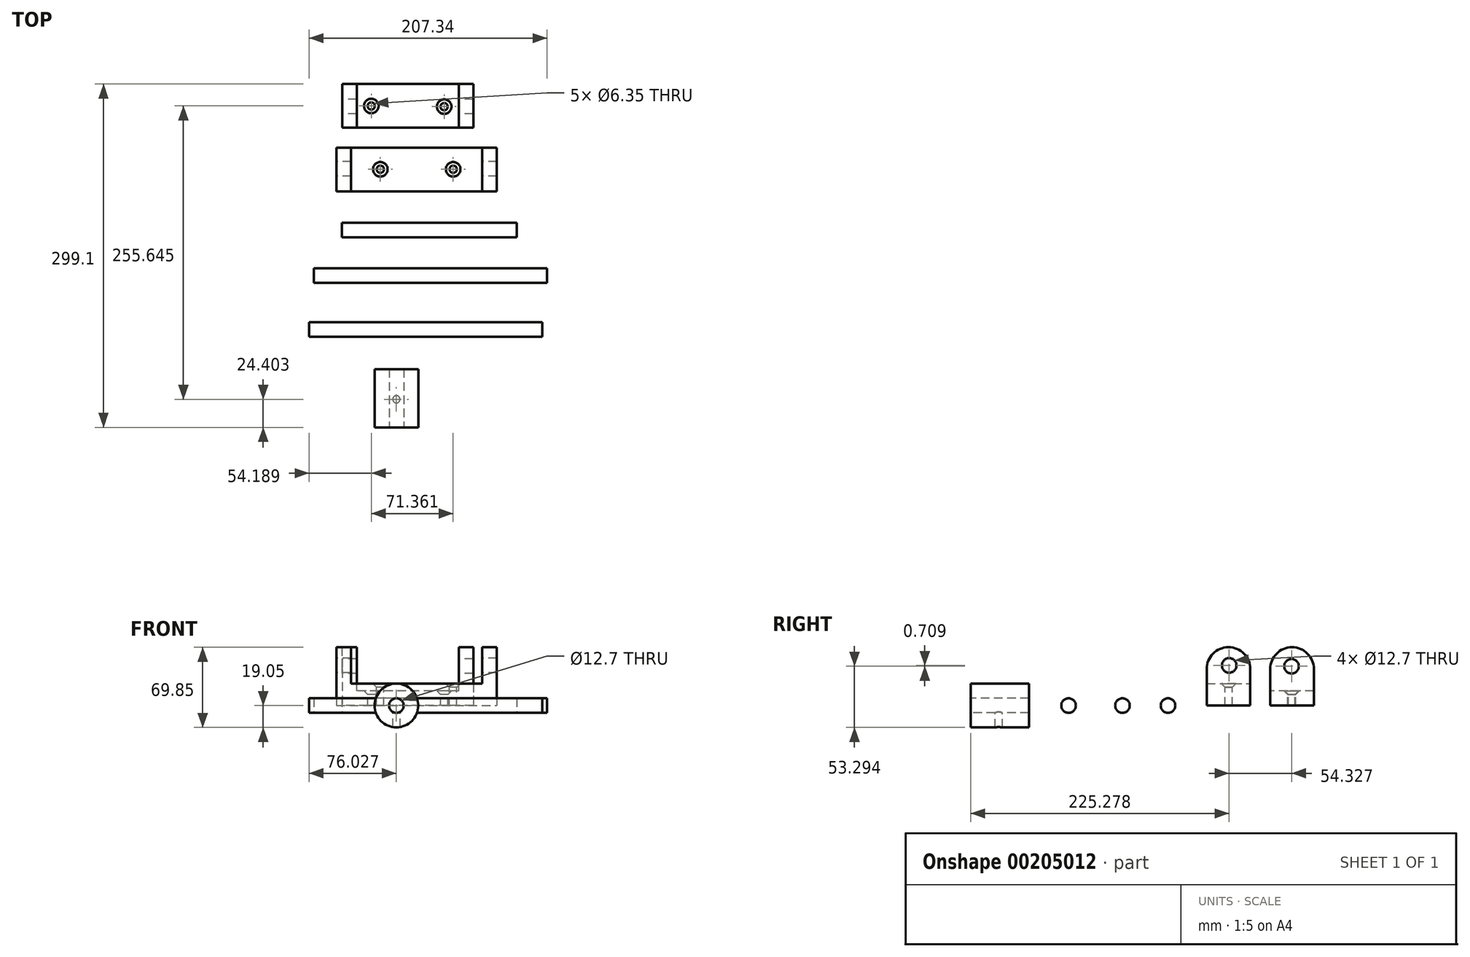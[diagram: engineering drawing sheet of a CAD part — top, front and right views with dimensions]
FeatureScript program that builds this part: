
annotation { "Feature Type Name" : "Feature", "Feature Type Description" : "" }
export const myFeature = defineFeature(function(context is Context, id is Id, definition is map)
    precondition{}
    {
        {
            var Q0;
            Q0=qCreatedBy(makeId("Top.planeOp"),FACE);
            var sketch = newSketch(context, id + "F0", { "sketchPlane" : qUnion([Q0])});
            skLineSegment(sketch, "E0.bottom", {"start": v(0, 38.1) * mm, "end": v(139.7, 38.1) * mm});
            skLineSegment(sketch, "E0.top", {"start": v(0, 0) * mm, "end": v(139.7, 0) * mm});
            skLineSegment(sketch, "E0.left", {"start": v(0, 38.1) * mm, "end": v(0, 0) * mm});
            skLineSegment(sketch, "E0.right", {"start": v(139.7, 38.1) * mm, "end": v(139.7, 0) * mm});
            skSolve(sketch);
        }
        {
            var Q0;
            Q0 = qSketchRegion(id + "F0", true);
            extrude(context, id + "F1", {"entities" : qUnion([Q0]), "depth" : 50.8 * mm});
        }
        {
            var Q0;
            Q0=makeQuery(id+"F1.opExtrude","CAP_FACE",FACE,{"disambiguationData":[OSD([sQuery(id+"F0.wireOp",EDGE,"E0.bottom"),sQuery(id+"F0.wireOp",EDGE,"E0.top"),sQuery(id+"F0.wireOp",EDGE,"E0.left"),sQuery(id+"F0.wireOp",EDGE,"E0.right")])],"isStart":false});
            var sketch = newSketch(context, id + "F2", { "sketchPlane" : qUnion([Q0])});
            skLineSegment(sketch, "E1.bottom", {"start": v(12.7, 0) * mm, "end": v(127, 0) * mm});
            skLineSegment(sketch, "E1.top", {"start": v(12.7, 38.1) * mm, "end": v(127, 38.1) * mm});
            skLineSegment(sketch, "E1.left", {"start": v(12.7, 0) * mm, "end": v(12.7, 38.1) * mm});
            skLineSegment(sketch, "E1.right", {"start": v(127, 0) * mm, "end": v(127, 38.1) * mm});
            skSolve(sketch);
        }
        {
            var Q0;
            Q0=makeQuery(id+"F2.imprint","IMPRINT",FACE,{"disambiguationData":[TD([[makeQuery(id+"F2.imprint","IMPRINT",EDGE,{"derivedFrom":sQuery(id+"F2.wireOp",EDGE,"E1.bottom")}),1.0]])]});
            extrude(context, id + "F3", {"entities" : qUnion([Q0]), "operationType" : NewBodyOperationType.REMOVE, "oppositeDirection" : true, "depth" : 31.75 * mm});
        }
        {
            var Q0;
            Q0=qCreatedBy(makeId("Right.planeOp"),FACE);
            var sketch = newSketch(context, id + "F4", { "sketchPlane" : qUnion([Q0])});
            skPoint(sketch, "E2", {"position": v(19.66, 34.95) * mm});
            skSolve(sketch);
        }
        {
            var Q0;
            Q0=sQuery(id+"F4.wireOp",VERTEX,"E2");
            var Q1;
            Q1=makeQuery(id+"F1.opExtrude","SWEPT_BODY",BODY,{"disambiguationData":[OSD([sQuery(id+"F0.wireOp",EDGE,"E0.bottom"),sQuery(id+"F0.wireOp",EDGE,"E0.top"),sQuery(id+"F0.wireOp",EDGE,"E0.left"),sQuery(id+"F0.wireOp",EDGE,"E0.right")])]});
            hole(context, id + "F5", {"style" : HoleStyle.SIMPLE, "endStyle" : HoleEndStyle.THROUGH, "oppositeDirection" : true, "holeDiameter" : 12.7 * mm, "locations" : qUnion([Q0]), "scope" : qUnion([Q1]), "isTappedThrough" : true});
        }
        {
            var Q0;
            Q0=makeQuery(id+"F3.boolean.opBoolean","COPY",FACE,{"derivedFrom":makeQuery(id+"F3.opExtrude","CAP_FACE",FACE,{"disambiguationData":[OSD([sQuery(id+"F2.wireOp",EDGE,"E1.bottom"),sQuery(id+"F2.wireOp",EDGE,"E1.top"),sQuery(id+"F2.wireOp",EDGE,"E1.left"),sQuery(id+"F2.wireOp",EDGE,"E1.right")])],"isStart":false})});
            var sketch = newSketch(context, id + "F6", { "sketchPlane" : qUnion([Q0])});
            skPoint(sketch, "E3", {"position": v(38.1, 19.3) * mm});
            skPoint(sketch, "E4", {"position": v(101.6, 19.3) * mm});
            skLineSegment(sketch, "E5", {"start": v(38.1, 19.3) * mm, "end": v(12.7, 19.05) * mm, "construction": true});
            skLineSegment(sketch, "E6", {"start": v(101.6, 19.3) * mm, "end": v(127, 19.05) * mm, "construction": true});
            skSolve(sketch);
        }
        {
            var Q0;
            Q0=sQuery(id+"F6.wireOp",VERTEX,"E3");
            var Q1;
            Q1=makeQuery(id+"F1.opExtrude","SWEPT_BODY",BODY,{"disambiguationData":[OSD([sQuery(id+"F0.wireOp",EDGE,"E0.bottom"),sQuery(id+"F0.wireOp",EDGE,"E0.top"),sQuery(id+"F0.wireOp",EDGE,"E0.left"),sQuery(id+"F0.wireOp",EDGE,"E0.right")])]});
            hole(context, id + "F7", {"style" : HoleStyle.C_SINK, "endStyle" : HoleEndStyle.THROUGH, "holeDiameter" : 6.35 * mm, "cSinkDiameter" : 12.7 * mm, "cSinkAngle" : 90 * degree, "locations" : qUnion([Q0]), "scope" : qUnion([Q1]), "isTappedThrough" : true});
        }
        {
            var Q0;
            Q0=sQuery(id+"F6.wireOp",VERTEX,"E4");
            var Q1;
            Q1=makeQuery(id+"F1.opExtrude","SWEPT_BODY",BODY,{"disambiguationData":[OSD([sQuery(id+"F0.wireOp",EDGE,"E0.bottom"),sQuery(id+"F0.wireOp",EDGE,"E0.top"),sQuery(id+"F0.wireOp",EDGE,"E0.left"),sQuery(id+"F0.wireOp",EDGE,"E0.right")])]});
            hole(context, id + "F8", {"style" : HoleStyle.C_SINK, "endStyle" : HoleEndStyle.THROUGH, "holeDiameter" : 6.35 * mm, "cSinkDiameter" : 12.7 * mm, "cSinkAngle" : 90 * degree, "locations" : qUnion([Q0]), "scope" : qUnion([Q1]), "isTappedThrough" : true});
        }
        {
            var Q0;
            Q0=qCreatedBy(makeId("Top.planeOp"),FACE);
            var sketch = newSketch(context, id + "F9", { "sketchPlane" : qUnion([Q0])});
            skLineSegment(sketch, "E7.bottom", {"start": v(119.14, 93.48) * mm, "end": v(4.84, 93.48) * mm});
            skLineSegment(sketch, "E7.top", {"start": v(119.14, 55.38) * mm, "end": v(4.84, 55.38) * mm});
            skLineSegment(sketch, "E7.left", {"start": v(119.14, 93.48) * mm, "end": v(119.14, 55.38) * mm});
            skLineSegment(sketch, "E7.right", {"start": v(4.84, 93.48) * mm, "end": v(4.84, 55.38) * mm});
            skSolve(sketch);
        }
        {
            var Q0;
            Q0=makeQuery(id+"F9.imprint","IMPRINT",FACE,{"disambiguationData":[TD([[makeQuery(id+"F9.imprint","IMPRINT",EDGE,{"derivedFrom":sQuery(id+"F9.wireOp",EDGE,"E7.bottom")}),1.0]])]});
            extrude(context, id + "F10", {"entities" : qUnion([Q0]), "depth" : 50.8 * mm});
        }
        {
            var Q0;
            Q0=makeQuery(id+"F10.opExtrude","CAP_FACE",FACE,{"disambiguationData":[OSD([sQuery(id+"F9.wireOp",EDGE,"E7.bottom"),sQuery(id+"F9.wireOp",EDGE,"E7.top"),sQuery(id+"F9.wireOp",EDGE,"E7.left"),sQuery(id+"F9.wireOp",EDGE,"E7.right")])],"isStart":false});
            var sketch = newSketch(context, id + "F11", { "sketchPlane" : qUnion([Q0])});
            skLineSegment(sketch, "E8.bottom", {"start": v(17.54, 93.48) * mm, "end": v(106.44, 93.48) * mm});
            skLineSegment(sketch, "E8.top", {"start": v(17.54, 55.38) * mm, "end": v(106.44, 55.38) * mm});
            skLineSegment(sketch, "E8.left", {"start": v(17.54, 93.48) * mm, "end": v(17.54, 55.38) * mm});
            skLineSegment(sketch, "E8.right", {"start": v(106.44, 93.48) * mm, "end": v(106.44, 55.38) * mm});
            skSolve(sketch);
        }
        {
            var Q0;
            Q0=makeQuery(id+"F11.imprint","IMPRINT",FACE,{"disambiguationData":[TD([[makeQuery(id+"F11.imprint","IMPRINT",EDGE,{"derivedFrom":sQuery(id+"F11.wireOp",EDGE,"E8.bottom")}),1.0]])]});
            extrude(context, id + "F12", {"entities" : qUnion([Q0]), "operationType" : NewBodyOperationType.REMOVE, "oppositeDirection" : true, "depth" : 38.1 * mm});
        }
        {
            var Q0;
            Q0=qCreatedBy(makeId("Right.planeOp"),FACE);
            var sketch = newSketch(context, id + "F13", { "sketchPlane" : qUnion([Q0])});
            skPoint(sketch, "E9", {"position": v(73.98, 34.24) * mm});
            skSolve(sketch);
        }
        {
            var Q0;
            Q0=sQuery(id+"F13.wireOp",VERTEX,"E9");
            var Q1;
            Q1=makeQuery(id+"F10.opExtrude","SWEPT_BODY",BODY,{"disambiguationData":[OSD([sQuery(id+"F9.wireOp",EDGE,"E7.bottom"),sQuery(id+"F9.wireOp",EDGE,"E7.top"),sQuery(id+"F9.wireOp",EDGE,"E7.left"),sQuery(id+"F9.wireOp",EDGE,"E7.right")])]});
            hole(context, id + "F14", {"style" : HoleStyle.SIMPLE, "endStyle" : HoleEndStyle.THROUGH, "oppositeDirection" : true, "holeDiameter" : 12.7 * mm, "locations" : qUnion([Q0]), "scope" : qUnion([Q1]), "isTappedThrough" : true});
        }
        {
            var Q0;
            Q0=makeQuery(id+"F12.boolean.opBoolean","COPY",FACE,{"derivedFrom":makeQuery(id+"F12.opExtrude","CAP_FACE",FACE,{"disambiguationData":[OSD([sQuery(id+"F11.wireOp",EDGE,"E8.bottom"),sQuery(id+"F11.wireOp",EDGE,"E8.top"),sQuery(id+"F11.wireOp",EDGE,"E8.left"),sQuery(id+"F11.wireOp",EDGE,"E8.right")])],"isStart":false})});
            var sketch = newSketch(context, id + "F15", { "sketchPlane" : qUnion([Q0])});
            skPoint(sketch, "E10", {"position": v(30.24, 74.43) * mm});
            skPoint(sketch, "E11", {"position": v(93.74, 73.86) * mm});
            skLineSegment(sketch, "E12", {"start": v(30.24, 74.43) * mm, "end": v(17.54, 74.43) * mm, "construction": true});
            skLineSegment(sketch, "E13", {"start": v(93.74, 73.86) * mm, "end": v(106.44, 73.86) * mm, "construction": true});
            skSolve(sketch);
        }
        {
            var Q0;
            Q0=sQuery(id+"F15.wireOp",VERTEX,"E10");
            var Q1;
            Q1=sQuery(id+"F15.wireOp",VERTEX,"E11");
            var Q2;
            Q2=makeQuery(id+"F10.opExtrude","SWEPT_BODY",BODY,{"disambiguationData":[OSD([sQuery(id+"F9.wireOp",EDGE,"E7.bottom"),sQuery(id+"F9.wireOp",EDGE,"E7.top"),sQuery(id+"F9.wireOp",EDGE,"E7.left"),sQuery(id+"F9.wireOp",EDGE,"E7.right")])]});
            hole(context, id + "F16", {"style" : HoleStyle.C_SINK, "endStyle" : HoleEndStyle.THROUGH, "holeDiameter" : 6.35 * mm, "cSinkDiameter" : 12.7 * mm, "cSinkAngle" : 90 * degree, "locations" : qUnion([Q0, Q1]), "scope" : qUnion([Q2]), "isTappedThrough" : true});
        }
        {
            var Q0;
            Q0=qCreatedBy(makeId("Top.planeOp"),FACE);
            var sketch = newSketch(context, id + "F17", { "sketchPlane" : qUnion([Q0])});
            skLineSegment(sketch, "E14.bottom", {"start": v(4.62, -27.31) * mm, "end": v(157.02, -27.31) * mm});
            skLineSegment(sketch, "E14.top", {"start": v(4.62, -33.66) * mm, "end": v(157.02, -33.66) * mm});
            skLineSegment(sketch, "E14.left", {"start": v(4.62, -27.31) * mm, "end": v(4.62, -33.66) * mm});
            skLineSegment(sketch, "E14.right", {"start": v(157.02, -27.31) * mm, "end": v(157.02, -33.66) * mm});
            skSolve(sketch);
        }
        {
            var Q0;
            Q0 = qSketchRegion(id + "F17", true);
            var Q1;
            Q1=sQuery(id+"F17.wireOp",EDGE,"E14.top");
            revolve(context, id + "F18", {"entities" : qUnion([Q0]), "axis" : qUnion([Q1]), "revolveType" : RevolveType.FULL});
        }
        {
            var Q0;
            {var subQ0=sQuery(id+"F9.wireOp",EDGE,"E7.bottom");var subQ1=sQuery(id+"F9.wireOp",EDGE,"E7.right");Q0=makeQuery(id+"F12.boolean.opBoolean","SPLIT",EDGE,{"disambiguationData":[TD([makeQuery(id+"F10.opExtrude","SWEPT_FACE",FACE,{"disambiguationData":[OSD([subQ1])]})])],"derivedFrom":makeQuery(id+"F10.opExtrude","CAP_EDGE",EDGE,{"disambiguationData":[OSD([subQ0])],"isStart":false})});}
            var Q1;
            {var subQ0=sQuery(id+"F9.wireOp",EDGE,"E7.right");var subQ1=sQuery(id+"F9.wireOp",EDGE,"E7.top");Q1=makeQuery(id+"F12.boolean.opBoolean","SPLIT",EDGE,{"disambiguationData":[TD([makeQuery(id+"F10.opExtrude","SWEPT_FACE",FACE,{"disambiguationData":[OSD([subQ0])]})])],"derivedFrom":makeQuery(id+"F10.opExtrude","CAP_EDGE",EDGE,{"disambiguationData":[OSD([subQ1])],"isStart":false})});}
            var Q2;
            {var subQ0=sQuery(id+"F0.wireOp",EDGE,"E0.bottom");var subQ1=sQuery(id+"F0.wireOp",EDGE,"E0.left");Q2=makeQuery(id+"F3.boolean.opBoolean","SPLIT",EDGE,{"disambiguationData":[TD([makeQuery(id+"F1.opExtrude","SWEPT_FACE",FACE,{"disambiguationData":[OSD([subQ1])]})])],"derivedFrom":makeQuery(id+"F1.opExtrude","CAP_EDGE",EDGE,{"disambiguationData":[OSD([subQ0])],"isStart":false})});}
            var Q3;
            {var subQ0=sQuery(id+"F0.wireOp",EDGE,"E0.left");var subQ1=sQuery(id+"F0.wireOp",EDGE,"E0.top");Q3=makeQuery(id+"F3.boolean.opBoolean","SPLIT",EDGE,{"disambiguationData":[TD([makeQuery(id+"F1.opExtrude","SWEPT_FACE",FACE,{"disambiguationData":[OSD([subQ0])]})])],"derivedFrom":makeQuery(id+"F1.opExtrude","CAP_EDGE",EDGE,{"disambiguationData":[OSD([subQ1])],"isStart":false})});}
            var Q4;
            {var subQ0=sQuery(id+"F0.wireOp",EDGE,"E0.bottom");var subQ1=sQuery(id+"F0.wireOp",EDGE,"E0.right");Q4=makeQuery(id+"F3.boolean.opBoolean","SPLIT",EDGE,{"disambiguationData":[TD([makeQuery(id+"F1.opExtrude","SWEPT_FACE",FACE,{"disambiguationData":[OSD([subQ1])]})])],"derivedFrom":makeQuery(id+"F1.opExtrude","CAP_EDGE",EDGE,{"disambiguationData":[OSD([subQ0])],"isStart":false})});}
            var Q5;
            {var subQ0=sQuery(id+"F0.wireOp",EDGE,"E0.right");var subQ1=sQuery(id+"F0.wireOp",EDGE,"E0.top");Q5=makeQuery(id+"F3.boolean.opBoolean","SPLIT",EDGE,{"disambiguationData":[TD([makeQuery(id+"F1.opExtrude","SWEPT_FACE",FACE,{"disambiguationData":[OSD([subQ0])]})])],"derivedFrom":makeQuery(id+"F1.opExtrude","CAP_EDGE",EDGE,{"disambiguationData":[OSD([subQ1])],"isStart":false})});}
            var Q6;
            {var subQ0=sQuery(id+"F9.wireOp",EDGE,"E7.left");var subQ1=sQuery(id+"F9.wireOp",EDGE,"E7.top");Q6=makeQuery(id+"F12.boolean.opBoolean","SPLIT",EDGE,{"disambiguationData":[TD([makeQuery(id+"F10.opExtrude","SWEPT_FACE",FACE,{"disambiguationData":[OSD([subQ0])]})])],"derivedFrom":makeQuery(id+"F10.opExtrude","CAP_EDGE",EDGE,{"disambiguationData":[OSD([subQ1])],"isStart":false})});}
            var Q7;
            {var subQ0=sQuery(id+"F9.wireOp",EDGE,"E7.bottom");var subQ1=sQuery(id+"F9.wireOp",EDGE,"E7.left");Q7=makeQuery(id+"F12.boolean.opBoolean","SPLIT",EDGE,{"disambiguationData":[TD([makeQuery(id+"F10.opExtrude","SWEPT_FACE",FACE,{"disambiguationData":[OSD([subQ1])]})])],"derivedFrom":makeQuery(id+"F10.opExtrude","CAP_EDGE",EDGE,{"disambiguationData":[OSD([subQ0])],"isStart":false})});}
            fillet(context, id + "F19", {"entities" : qUnion([Q0, Q1, Q2, Q3, Q4, Q5, Q6, Q7]), "radius" : 19.05 * mm, "tangentPropagation" : true, "allowEdgeOverflow" : false});
        }
        {
            var Q0;
            Q0=qCreatedBy(makeId("Top.planeOp"),FACE);
            var sketch = newSketch(context, id + "F20", { "sketchPlane" : qUnion([Q0])});
            skLineSegment(sketch, "E15.bottom", {"start": v(-19.81, -67.01) * mm, "end": v(183.39, -67.01) * mm});
            skLineSegment(sketch, "E15.top", {"start": v(-19.81, -73.36) * mm, "end": v(183.39, -73.36) * mm});
            skLineSegment(sketch, "E15.left", {"start": v(-19.81, -67.01) * mm, "end": v(-19.81, -73.36) * mm});
            skLineSegment(sketch, "E15.right", {"start": v(183.39, -67.01) * mm, "end": v(183.39, -73.36) * mm});
            skSolve(sketch);
        }
        {
            var Q0;
            Q0=makeQuery(id+"F20.imprint","IMPRINT",FACE,{"disambiguationData":[TD([[makeQuery(id+"F20.imprint","IMPRINT",EDGE,{"derivedFrom":sQuery(id+"F20.wireOp",EDGE,"E15.bottom")}),-1.0]])]});
            var Q1;
            Q1=sQuery(id+"F20.wireOp",EDGE,"E15.top");
            revolve(context, id + "F21", {"entities" : qUnion([Q0]), "axis" : qUnion([Q1]), "revolveType" : RevolveType.FULL});
        }
        {
            var Q0;
            Q0=qCreatedBy(makeId("Top.planeOp"),FACE);
            var sketch = newSketch(context, id + "F22", { "sketchPlane" : qUnion([Q0])});
            skLineSegment(sketch, "E16.bottom", {"start": v(-23.95, -113.97) * mm, "end": v(179.25, -113.97) * mm});
            skLineSegment(sketch, "E16.top", {"start": v(-23.95, -120.32) * mm, "end": v(179.25, -120.32) * mm});
            skLineSegment(sketch, "E16.left", {"start": v(-23.95, -113.97) * mm, "end": v(-23.95, -120.32) * mm});
            skLineSegment(sketch, "E16.right", {"start": v(179.25, -113.97) * mm, "end": v(179.25, -120.32) * mm});
            skSolve(sketch);
        }
        {
            var Q0;
            Q0=makeQuery(id+"F22.imprint","IMPRINT",FACE,{"disambiguationData":[TD([[makeQuery(id+"F22.imprint","IMPRINT",EDGE,{"derivedFrom":sQuery(id+"F22.wireOp",EDGE,"E16.bottom")}),-1.0]])]});
            var Q1;
            Q1=sQuery(id+"F22.wireOp",EDGE,"E16.top");
            revolve(context, id + "F23", {"entities" : qUnion([Q0]), "axis" : qUnion([Q1]), "revolveType" : RevolveType.FULL});
        }
        {
            var Q0;
            Q0=qCreatedBy(makeId("Top.planeOp"),FACE);
            var sketch = newSketch(context, id + "F24", { "sketchPlane" : qUnion([Q0])});
            skLineSegment(sketch, "E17.bottom", {"start": v(33.03, -154.82) * mm, "end": v(52.08, -154.82) * mm});
            skLineSegment(sketch, "E17.top", {"start": v(33.03, -205.62) * mm, "end": v(52.08, -205.62) * mm});
            skLineSegment(sketch, "E17.left", {"start": v(33.03, -154.82) * mm, "end": v(33.03, -205.62) * mm});
            skLineSegment(sketch, "E17.right", {"start": v(52.08, -154.82) * mm, "end": v(52.08, -205.62) * mm});
            skPoint(sketch, "E18.positionSnap0", {"position": v(42.55, -154.82) * mm});
            skPoint(sketch, "E19", {"position": v(52.08, -181.22) * mm});
            skSolve(sketch);
        }
        {
            var Q0;
            Q0=makeQuery(id+"F24.imprint","IMPRINT",FACE,{"disambiguationData":[TD([[makeQuery(id+"F24.imprint","IMPRINT",EDGE,{"derivedFrom":sQuery(id+"F24.wireOp",EDGE,"E17.bottom")}),-1.0]])]});
            var Q1;
            Q1=sQuery(id+"F24.wireOp",EDGE,"E17.right");
            revolve(context, id + "F25", {"entities" : qUnion([Q0]), "axis" : qUnion([Q1]), "revolveType" : RevolveType.FULL});
        }
        {
            var Q0;
            Q0=makeQuery(id+"F25.opRevolve","SWEPT_FACE",FACE,{"disambiguationData":[OSD([sQuery(id+"F24.wireOp",EDGE,"E17.top")])]});
            var sketch = newSketch(context, id + "F26", { "sketchPlane" : qUnion([Q0])});
            skPoint(sketch, "E20", {"position": v(52.08, 0) * mm});
            skSolve(sketch);
        }
        {
            var Q0;
            Q0=sQuery(id+"F24.wireOp",VERTEX,"E19");
            var Q1;
            Q1=makeQuery(id+"F25.opRevolve","SWEPT_BODY",BODY,{"disambiguationData":[OSD([sQuery(id+"F24.wireOp",EDGE,"E17.bottom"),sQuery(id+"F24.wireOp",EDGE,"E17.top"),sQuery(id+"F24.wireOp",EDGE,"E17.left"),sQuery(id+"F24.wireOp",EDGE,"E17.right")])]});
            hole(context, id + "F27", {"style" : HoleStyle.SIMPLE, "endStyle" : HoleEndStyle.THROUGH, "holeDiameter" : 6.35 * mm, "locations" : qUnion([Q0]), "scope" : qUnion([Q1]), "isTappedThrough" : true});
        }
        {
            var Q0;
            Q0=sQuery(id+"F26.wireOp",VERTEX,"E20");
            var Q1;
            Q1=makeQuery(id+"F25.opRevolve","SWEPT_BODY",BODY,{"disambiguationData":[OSD([sQuery(id+"F24.wireOp",EDGE,"E17.bottom"),sQuery(id+"F24.wireOp",EDGE,"E17.top"),sQuery(id+"F24.wireOp",EDGE,"E17.left"),sQuery(id+"F24.wireOp",EDGE,"E17.right")])]});
            hole(context, id + "F28", {"style" : HoleStyle.SIMPLE, "endStyle" : HoleEndStyle.THROUGH, "holeDiameter" : 12.7 * mm, "locations" : qUnion([Q0]), "scope" : qUnion([Q1]), "isTappedThrough" : true});
        }
    });
